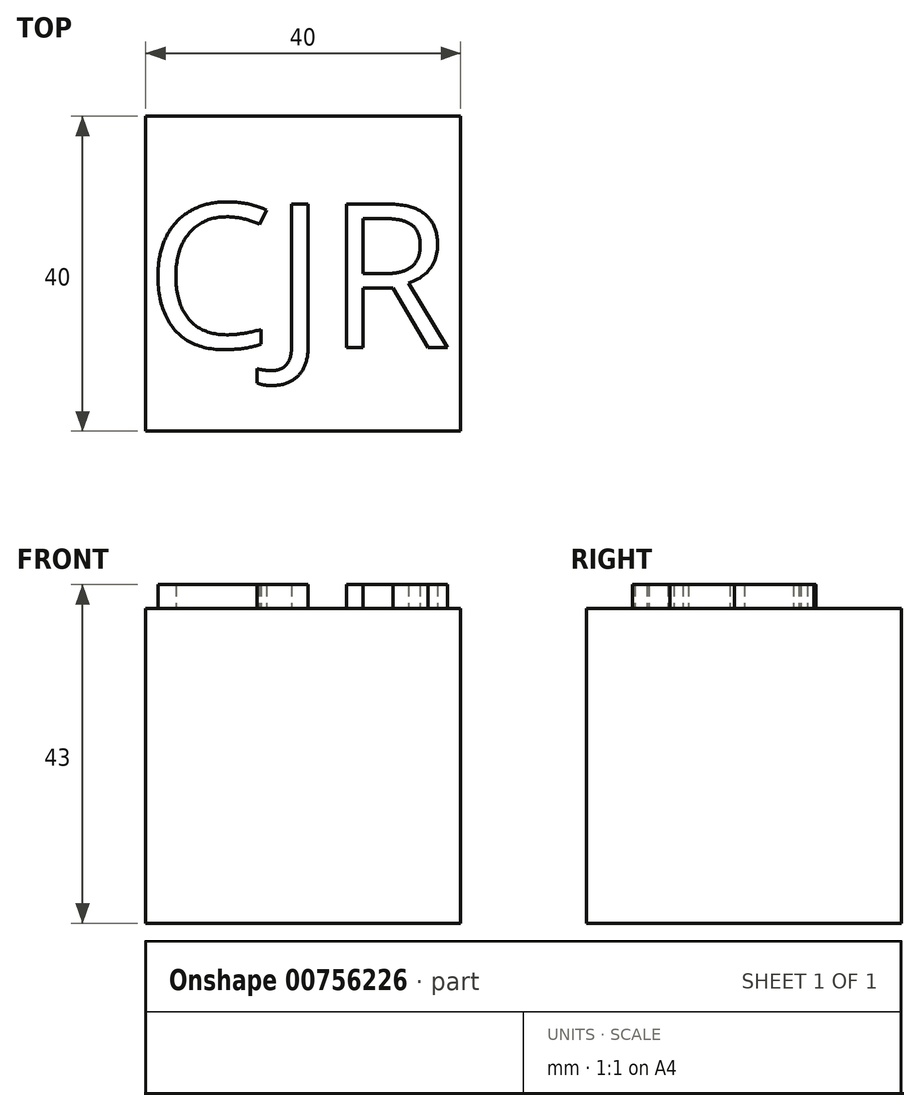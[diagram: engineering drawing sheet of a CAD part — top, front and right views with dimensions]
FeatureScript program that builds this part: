
annotation { "Feature Type Name" : "Feature", "Feature Type Description" : "" }
export const myFeature = defineFeature(function(context is Context, id is Id, definition is map)
    precondition{}
    {
        {
            var Q0;
            Q0=qCreatedBy(makeId("Front.planeOp"),FACE);
            var sketch = newSketch(context, id + "F0", { "sketchPlane" : qUnion([Q0])});
            skLineSegment(sketch, "E0", {"start": v(0, 0) * mm, "end": v(0, 40) * mm});
            skLineSegment(sketch, "E1", {"start": v(0, 40) * mm, "end": v(40, 40) * mm});
            skLineSegment(sketch, "E2", {"start": v(40, 40) * mm, "end": v(40, 0) * mm});
            skLineSegment(sketch, "E3", {"start": v(40, 0) * mm, "end": v(0, 0) * mm});
            skSolve(sketch);
        }
        {
            var Q0;
            Q0=makeQuery(id+"F0.imprint","IMPRINT",FACE,{"disambiguationData":[TD([[makeQuery(id+"F0.imprint","IMPRINT",EDGE,{"derivedFrom":sQuery(id+"F0.wireOp",EDGE,"E0")}),-1.0]])]});
            extrude(context, id + "F1", {"entities" : qUnion([Q0]), "oppositeDirection" : true, "depth" : 40 * mm, "offsetDistance" : 25 * mm});
        }
        {
            var Q0;
            Q0=makeQuery(id+"F1.opExtrude","SWEPT_FACE",FACE,{"disambiguationData":[OSD([sQuery(id+"F0.wireOp",EDGE,"E1")])]});
            var sketch = newSketch(context, id + "F2", { "sketchPlane" : qUnion([Q0])});
            skText(sketch, "E4", { "text": "CJR\n", "fontName": "OpenSans-Regular.ttf"});
            const initialGuessF2  = {"E4": [0, 0.01061, 1, 0, 0.01842]};
            skSetInitialGuess(sketch, initialGuessF2);
            skSolve(sketch);
        }
        {
            var Q0;
            Q0 = qSketchRegion(id + "F2", true);
            extrude(context, id + "F3", {"entities" : qUnion([Q0]), "operationType" : NewBodyOperationType.ADD, "depth" : 3 * mm, "offsetDistance" : 25 * mm});
        }
    });
